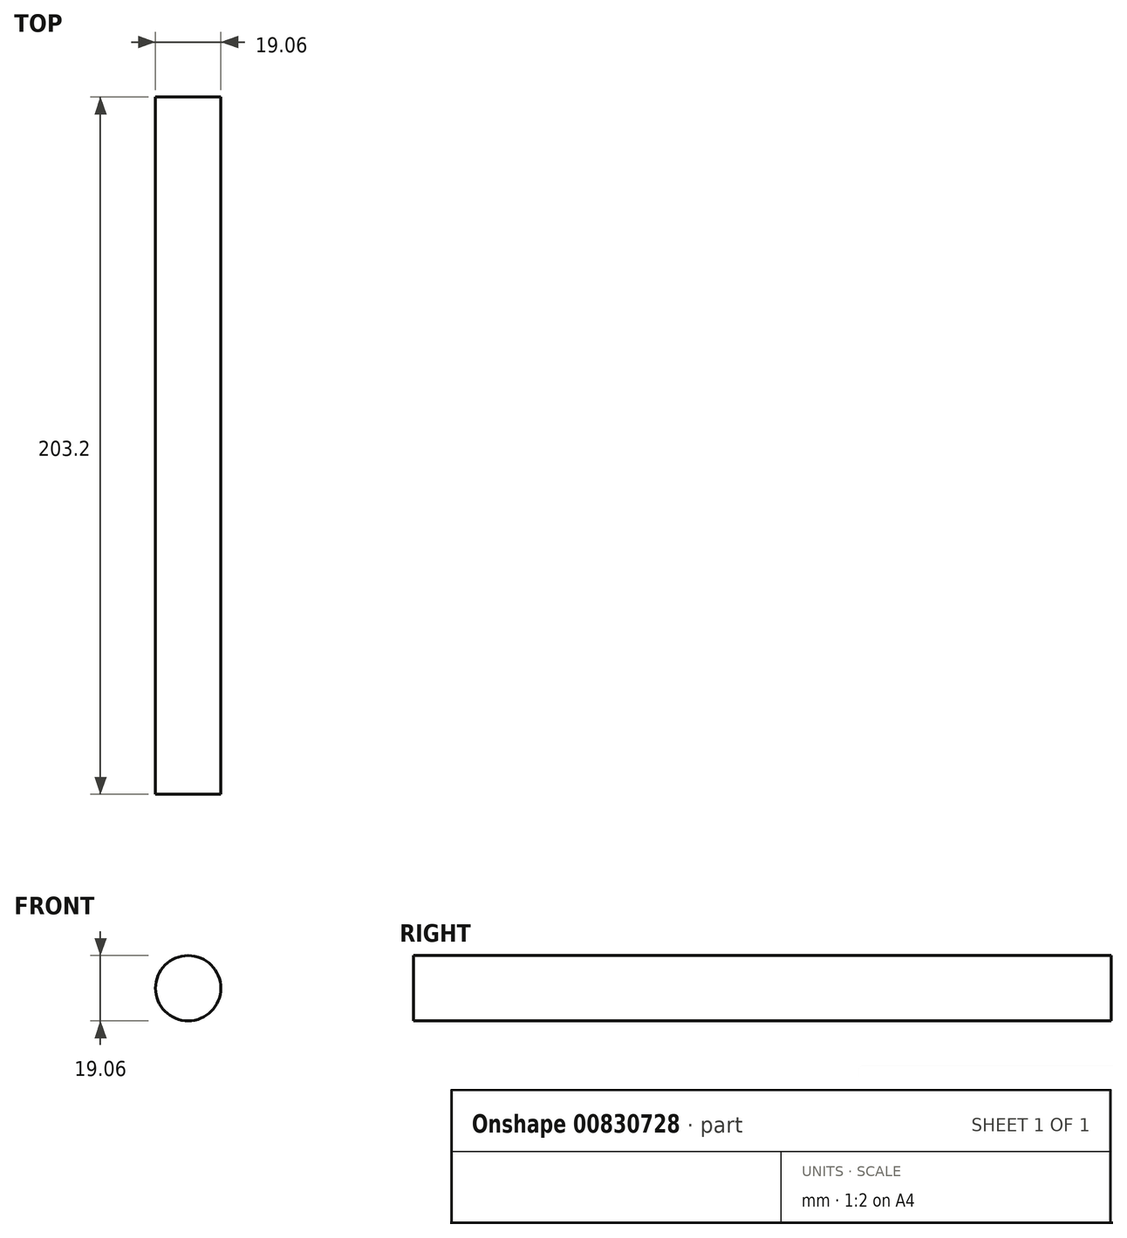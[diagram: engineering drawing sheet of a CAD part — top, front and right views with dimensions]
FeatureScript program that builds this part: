
annotation { "Feature Type Name" : "Feature", "Feature Type Description" : "" }
export const myFeature = defineFeature(function(context is Context, id is Id, definition is map)
    precondition{}
    {
        {
            var Q0;
            Q0=qCreatedBy(makeId("Front.planeOp"),FACE);
            var sketch = newSketch(context, id + "F0", { "sketchPlane" : qUnion([Q0])});
            skCircle(sketch, "E0", {"center": v(0, 0) * mm, "radius": 9.53 * mm});
            skSolve(sketch);
        }
        {
            var Q0;
            Q0 = qSketchRegion(id + "F0", true);
            extrude(context, id + "F1", {"entities" : qUnion([Q0]), "depth" : 203.2 * mm, "offsetDistance" : 25.4 * mm});
        }
    });
